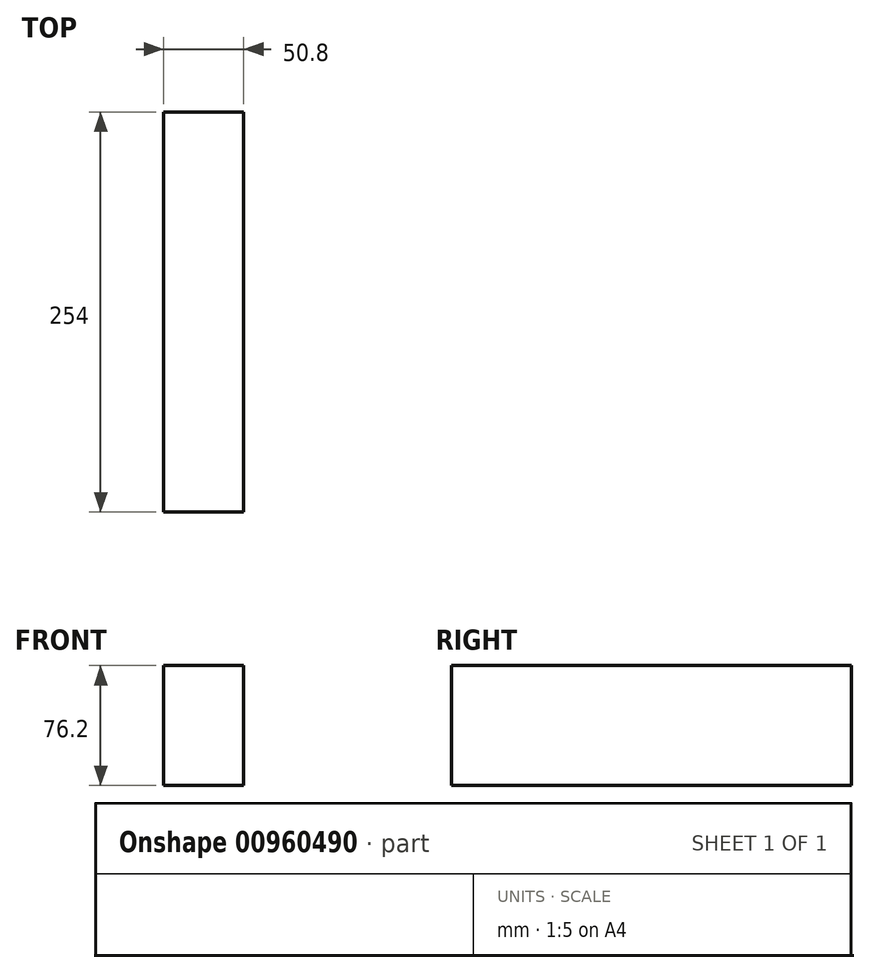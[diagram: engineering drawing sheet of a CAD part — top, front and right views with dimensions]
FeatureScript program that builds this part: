
annotation { "Feature Type Name" : "Feature", "Feature Type Description" : "" }
export const myFeature = defineFeature(function(context is Context, id is Id, definition is map)
    precondition{}
    {
        {
            var Q0;
            Q0=qCreatedBy(makeId("Front.planeOp"),FACE);
            var sketch = newSketch(context, id + "F0", { "sketchPlane" : qUnion([Q0])});
            skLineSegment(sketch, "E0.bottom", {"start": v(25.4, -38.1) * mm, "end": v(-25.4, -38.1) * mm});
            skLineSegment(sketch, "E0.top", {"start": v(25.4, 38.1) * mm, "end": v(-25.4, 38.1) * mm});
            skLineSegment(sketch, "E0.left", {"start": v(25.4, -38.1) * mm, "end": v(25.4, 38.1) * mm});
            skLineSegment(sketch, "E0.right", {"start": v(-25.4, -38.1) * mm, "end": v(-25.4, 38.1) * mm});
            skPoint(sketch, "E0.middle", {"position": v(0, 0) * mm});
            skSolve(sketch);
        }
        {
            var Q0;
            Q0=makeQuery(id+"F0.imprint","IMPRINT",FACE,{"disambiguationData":[TD([[makeQuery(id+"F0.imprint","IMPRINT",EDGE,{"derivedFrom":sQuery(id+"F0.wireOp",EDGE,"E0.bottom")}),-1.0]])]});
            extrude(context, id + "F1", {"entities" : qUnion([Q0]), "depth" : 254 * mm, "offsetDistance" : 25.4 * mm});
        }
    });
